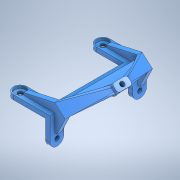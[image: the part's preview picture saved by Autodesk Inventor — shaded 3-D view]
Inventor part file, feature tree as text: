
AUTODESK INVENTOR PART (.ipt)
format: ipt  version: 2022 (Build 260153000, 153)  size: 571,392 bytes
history: native  units: mm
features: sketch x15, extrude x12, fillet x4, plane x3, hole x3, other x2, mirror x1, loft x1
ambient origin geometry x8: Origin, YZ Plane, XZ Plane, XY Plane, X Axis, Y Axis, Z Axis, Center Point
bodies: Body1 (feature_tree)
feature tree (41):
  extrude  "Extrusion6"  Depth=4.0mm
  plane  "Work Plane1"
  extrude  "Extrusion7"  Depth=2.0mm
  extrude  "Extrusion8"  Depth=28.504mm
  extrude  "Extrusion11"  Depth=6.362mm
  extrude  "Extrusion13"  Depth=24.240684mm
  hole  "Hole1"  [1 undecoded]
  plane  "Work Plane3"
  extrude  "Extrusion14"  Depth=6.5mm TaperAngle=0.0deg
  extrude  "Extrusion15"  Depth=2.0mm
  hole  "Hole2"  [1 undecoded]
  extrude  "Extrusion16"  Depth=1.0mm
  extrude  "Extrusion17"  Depth=1.0mm
  mirror  "Mirror1"
  extrude  "Extrusion18"  Depth=1.0mm
  loft  "Loft2"
  extrude  "Extrusion19"  Depth=10.0mm
  extrude  "Extrusion20"  Depth=4.0mm TaperAngle=0.0deg
  hole  "Hole3"  [1 undecoded]
  fillet  "Fillet1"  Radius=1.0mm
  fillet  "Fillet2"  Radius=2.0mm
  fillet  "Fillet3"  Radius=2.0mm
  fillet  "Fillet4"  Radius=1.0mm
  sketch  "Sketch7"  dims[d36=4.0mm d37=4.0mm]
  sketch  "Sketch9"  dims[d38=2.0mm d39=2.0mm]
  sketch  "Sketch10"  dims[d43=42.0mm d44=0.0mm d45=28.504mm]
  sketch  "Sketch14"  dims[d46=12.753mm d47=6.362mm]
  sketch  "Sketch16"  dims[d48=7.0mm d49=24.240684mm]
  sketch  "Sketch17"  dims[d50=1.5mm d51=90.0deg]
  sketch  "Sketch18"  dims[d52=3.5mm d53=6.5mm d54=0.0mm]
  sketch  "Sketch19"  dims[d55=2.0mm d56=2.0mm]
  sketch  "Sketch20"  dims[d57=2.0mm d58=2.0mm]
  sketch  "Sketch21"  dims[d59=1.0mm d60=1.0mm]
  sketch  "Sketch22"  dims[d61=1.0mm d62=1.0mm]
  plane  "Work Plane4"
  sketch  "Sketch23"  dims[d63=1.0mm d64=1.0mm]
  other  "Edges3"
  other  "Edges4"
  sketch  "Sketch24"  dims[d65=1.0mm d66=1.0mm]
  sketch  "Sketch27"  dims[d67=6.5mm d68=0.0mm d82=10.0mm]
  sketch  "Sketch28"  dims[d85=16.0mm d86=6.0mm d87=0.0mm d92=6.0mm d93=0.0mm d94=2.0mm d95=6.0mm d96=5.0mm d97=1.0mm d98=90.0deg d99=8.0mm d100=20.594885mm d101=1.0mm d102=2.0mm d103=0.0mm d104=2.0mm d105=0.0mm d106=2.0mm d107=6.0mm d108=5.0mm d109=1.0mm d110=90.0deg d111=8.0mm d112=20.594885mm d113=1.0mm d115=2.0mm d116=0.0mm d117=2.0mm d118=0.0mm d119=1.0mm d120=1.0mm d121=4.0mm d122=0.0mm d123=0.0mm d124=90.0deg d125=0.0mm d126=90.0deg d127=3.0mm d129=2.0mm d130=17.0mm d131=40.0mm d133=5.0mm d134=40.0mm d136=5.0mm d139=4.0mm d140=0.0mm d144=1.75mm d145=3.25mm d146=3.5mm d147=7.0mm d148=0.0mm d149=2.0mm d150=6.0mm d151=4.0mm d152=2.0mm d153=90.0deg d154=5.0mm d155=20.594885mm d156=3.0mm d157=2.0mm d158=1.0mm d159=4.0mm]
note: 3 required parameter values undecoded (feature->parameter linkage not recoverable at this tier; creation-order binding heuristic only, values carry confidence <= 0.55)
